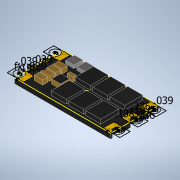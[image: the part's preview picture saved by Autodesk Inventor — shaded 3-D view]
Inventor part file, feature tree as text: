
AUTODESK INVENTOR PART (.ipt)
format: ipt  version: 2022 (Build 260153000, 153)  size: 355,328 bytes
history: native  units: in
note: dims shown in document units (in); Inventor stores cm internally (conversion verified against a paired STEP export)
features: extrude x6, sketch x5, mirror x1
ambient origin geometry x8: Origin, YZ Plane, XZ Plane, XY Plane, X Axis, Y Axis, Z Axis, Center Point
bodies: Solid1 (feature_tree)
feature tree (12):
  extrude  "Extrusion1"  Depth=0.6299in
  sketch  "Sketch2"  dims[d2=0.0344in d3=0.0in d4=0.0394in]
  extrude  "Extrusion2"  Depth=0.0394in
  extrude  "Extrusion3"  Depth=0.7874in
  mirror  "Mirror1"
  extrude  "Extrusion4"  Depth=0.1378in
  extrude  "Extrusion5"  Depth=0.0394in
  extrude  "Extrusion6"  Depth=0.1575in
  sketch  "Sketch1"  dims[d0=1.2598in d1=0.6299in]
  sketch  "Sketch3"  dims[d5=0.1181in d6=0.7874in d8=0.2362in d9=0.3937in d11=1.0in]
  sketch  "Sketch4"  dims[d13=0.2165in d14=0.1378in]
  sketch  "Sketch5"  dims[d15=0.7874in d17=0.2362in d18=0.3937in d20=1.0in d22=0.0394in d23=0.1575in d24=0.0689in d25=0.0in d26=0.0004in d27=0.0in d28=0.0197in d29=0.0197in d30=0.1969in d31=0.2362in d32=0.1673in d33=0.0394in d34=1.1811in d36=0.2264in d37=0.3937in d39=1.0in d41=0.0531in d42=0.0in d43=0.1083in d44=0.1181in d45=0.0197in d46=0.1772in d47=0.7874in d49=0.1476in d50=0.3937in d52=1.0in d54=0.0394in d55=0.0in d56=0.1122in d57=0.0689in d58=1.5748in d60=0.0846in d61=0.3937in d63=1.0in d65=0.0984in d66=0.1575in d67=0.1181in d68=0.1181in d69=0.1713in d70=0.315in d71=0.0787in d72=0.0394in d73=0.3543in d74=0.3346in d75=0.0591in d76=0.0in]
